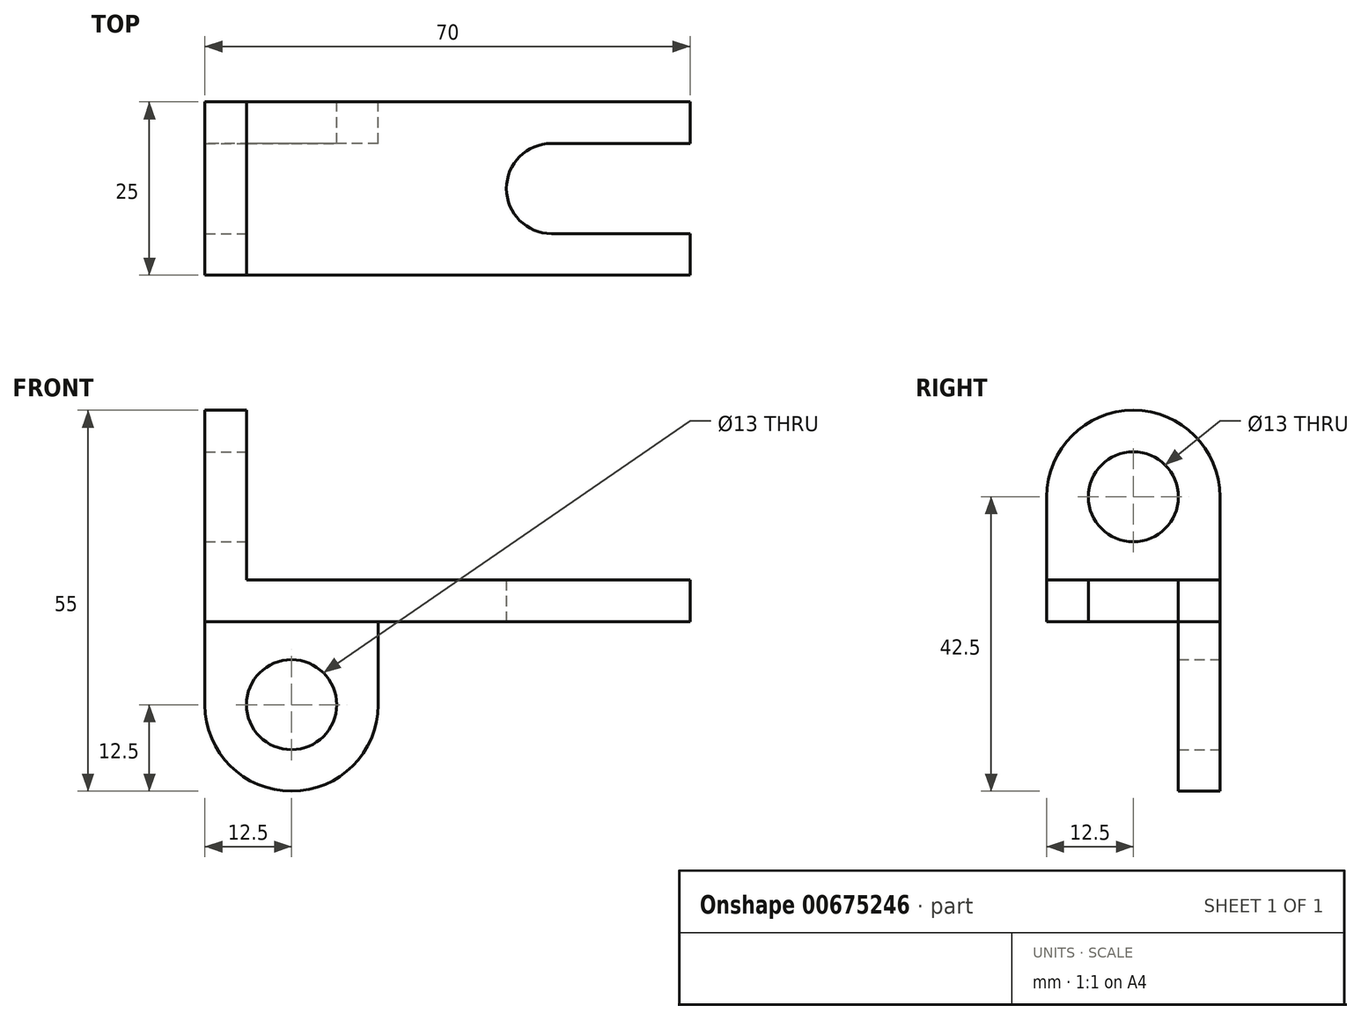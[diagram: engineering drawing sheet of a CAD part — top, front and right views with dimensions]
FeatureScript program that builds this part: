
annotation { "Feature Type Name" : "Feature", "Feature Type Description" : "" }
export const myFeature = defineFeature(function(context is Context, id is Id, definition is map)
    precondition{}
    {
        {
            var Q0;
            Q0=qCreatedBy(makeId("Top.planeOp"),FACE);
            var sketch = newSketch(context, id + "F0", { "sketchPlane" : qUnion([Q0])});
            skLineSegment(sketch, "E0.bottom", {"start": v(32, -12.5) * mm, "end": v(-32, -12.5) * mm});
            skLineSegment(sketch, "E0.top", {"start": v(32, 12.5) * mm, "end": v(-32, 12.5) * mm});
            skLineSegment(sketch, "E0.left", {"start": v(32, -12.5) * mm, "end": v(32, 12.5) * mm});
            skLineSegment(sketch, "E0.right", {"start": v(-32, -12.5) * mm, "end": v(-32, 12.5) * mm});
            skPoint(sketch, "E0.middle", {"position": v(0, 0) * mm});
            skLineSegment(sketch, "E1.bottom", {"start": v(32, -6.5) * mm, "end": v(12, -6.5) * mm});
            skLineSegment(sketch, "E1.top", {"start": v(32, 6.5) * mm, "end": v(12, 6.5) * mm});
            skLineSegment(sketch, "E1.left", {"start": v(32, -6.5) * mm, "end": v(32, 6.5) * mm});
            skLineSegment(sketch, "E1.right", {"start": v(12, -6.5) * mm, "end": v(12, 6.5) * mm});
            skPoint(sketch, "E1.middle", {"position": v(22, 0) * mm});
            skCircle(sketch, "E2", {"center": v(12, 0) * mm, "radius": 6.5 * mm});
            skSolve(sketch);
        }
        {
            var Q0;
            {var subQ4=sQuery(id+"F0.wireOp",EDGE,"E0.bottom");Q0=makeQuery(id+"F0.imprint","IMPRINT",FACE,{"disambiguationData":[TD([[makeQuery(id+"F0.imprint","IMPRINT",EDGE,{"derivedFrom":subQ4}),-1.0]])]});}
            extrude(context, id + "F1", {"entities" : qUnion([Q0]), "depth" : 6 * mm, "offsetDistance" : 25 * mm});
        }
        {
            var Q0;
            Q0=makeQuery(id+"F1.opExtrude","SWEPT_FACE",FACE,{"disambiguationData":[OSD([sQuery(id+"F0.wireOp",EDGE,"E0.right")])]});
            var sketch = newSketch(context, id + "F2", { "sketchPlane" : qUnion([Q0])});
            skLineSegment(sketch, "E3.bottom", {"start": v(12.5, 0) * mm, "end": v(-12.5, 0) * mm});
            skLineSegment(sketch, "E3.top", {"start": v(12.5, 18) * mm, "end": v(6.5, 18) * mm, "construction": true});
            skLineSegment(sketch, "E3.left", {"start": v(12.5, 0) * mm, "end": v(12.5, 18) * mm});
            skLineSegment(sketch, "E3.right", {"start": v(-12.5, 0) * mm, "end": v(-12.5, 18) * mm});
            skArc(sketch, "E4", {"start": v(12.5, 18) * mm, "mid": v(0, 30.5) * mm, "end": v(-12.5, 18) * mm});
            skCircle(sketch, "E5", {"center": v(0, 18) * mm, "radius": 6.5 * mm});
            skLineSegment(sketch, "E6.trimOffspring", {"start": v(-6.5, 18) * mm, "end": v(-12.5, 18) * mm, "construction": true});
            skSolve(sketch);
        }
        {
            var Q0;
            {var subQ0=sQuery(id+"F2.wireOp",EDGE,"E4");Q0=makeQuery(id+"F2.imprint","IMPRINT",FACE,{"disambiguationData":[TD([[makeQuery(id+"F2.imprint","IMPRINT",EDGE,{"derivedFrom":subQ0}),1.0]])]});}
            var Q1;
            {var subQ0=sQuery(id+"F2.wireOp",EDGE,"E3.bottom");Q1=makeQuery(id+"F2.imprint","IMPRINT",FACE,{"disambiguationData":[TD([[makeQuery(id+"F2.imprint","IMPRINT",EDGE,{"derivedFrom":subQ0}),-1.0]])]});}
            extrude(context, id + "F3", {"entities" : qUnion([Q0, Q1]), "operationType" : NewBodyOperationType.ADD, "depth" : 6 * mm, "offsetDistance" : 25 * mm});
        }
        {
            var Q0;
            Q0=makeQuery(id+"F3.boolean.opBoolean","MERGE",FACE,{"derivedFrom":[makeQuery(id+"F1.opExtrude","SWEPT_FACE",FACE,{"disambiguationData":[OSD([sQuery(id+"F0.wireOp",EDGE,"E0.top")])]}),makeQuery(id+"F3.opExtrude","SWEPT_FACE",FACE,{"disambiguationData":[OSD([sQuery(id+"F2.wireOp",EDGE,"E3.right")])]})]});
            var sketch = newSketch(context, id + "F4", { "sketchPlane" : qUnion([Q0])});
            skLineSegment(sketch, "E7.bottom", {"start": v(38, 6) * mm, "end": v(13, 6) * mm});
            skLineSegment(sketch, "E7.top", {"start": v(38, -12) * mm, "end": v(13, -12) * mm});
            skLineSegment(sketch, "E7.left", {"start": v(38, 6) * mm, "end": v(38, -12) * mm});
            skLineSegment(sketch, "E7.right", {"start": v(13, 6) * mm, "end": v(13, -12) * mm});
            skArc(sketch, "E8", {"start": v(13, -12) * mm, "mid": v(25.5, -24.5) * mm, "end": v(38, -12) * mm});
            skSolve(sketch);
        }
        {
            var Q0;
            {var subQ0=sQuery(id+"F4.wireOp",EDGE,"E7.top");Q0=makeQuery(id+"F4.imprint","IMPRINT",FACE,{"disambiguationData":[TD([[makeQuery(id+"F4.imprint","IMPRINT",EDGE,{"derivedFrom":subQ0}),-1.0]])]});}
            var Q1;
            Q1=makeQuery(id+"F4.imprint","IMPRINT",FACE,{"disambiguationData":[TD([[makeQuery(id+"F4.imprint","IMPRINT",EDGE,{"derivedFrom":sQuery(id+"F4.wireOp",EDGE,"E7.top")}),1.0]])]});
            extrude(context, id + "F5", {"entities" : qUnion([Q0, Q1]), "operationType" : NewBodyOperationType.ADD, "oppositeDirection" : true, "depth" : 6 * mm, "offsetDistance" : 25 * mm});
        }
        {
            var Q0;
            Q0=sQuery(id+"F4.wireOp",VERTEX,"E8.center");
            var Q1;
            Q1=makeQuery(id+"F1.opExtrude","SWEPT_BODY",BODY,{"disambiguationData":[OSD([sQuery(id+"F0.wireOp",EDGE,"E0.bottom"),sQuery(id+"F0.wireOp",EDGE,"E0.top"),sQuery(id+"F0.wireOp",EDGE,"E0.left"),sQuery(id+"F0.wireOp",EDGE,"E0.right"),sQuery(id+"F0.wireOp",EDGE,"E1.bottom"),sQuery(id+"F0.wireOp",EDGE,"E1.top"),sQuery(id+"F0.wireOp",EDGE,"E2")])]});
            hole(context, id + "F6", {"style" : HoleStyle.SIMPLE, "endStyle" : HoleEndStyle.THROUGH, "holeDiameter" : 13 * mm, "majorDiameter" : 5 * mm, "isTappedThrough" : true, "tappedDepth" : 12 * mm, "tapClearance" : 3, "locations" : qUnion([Q0]), "scope" : qUnion([Q1])});
        }
    });
